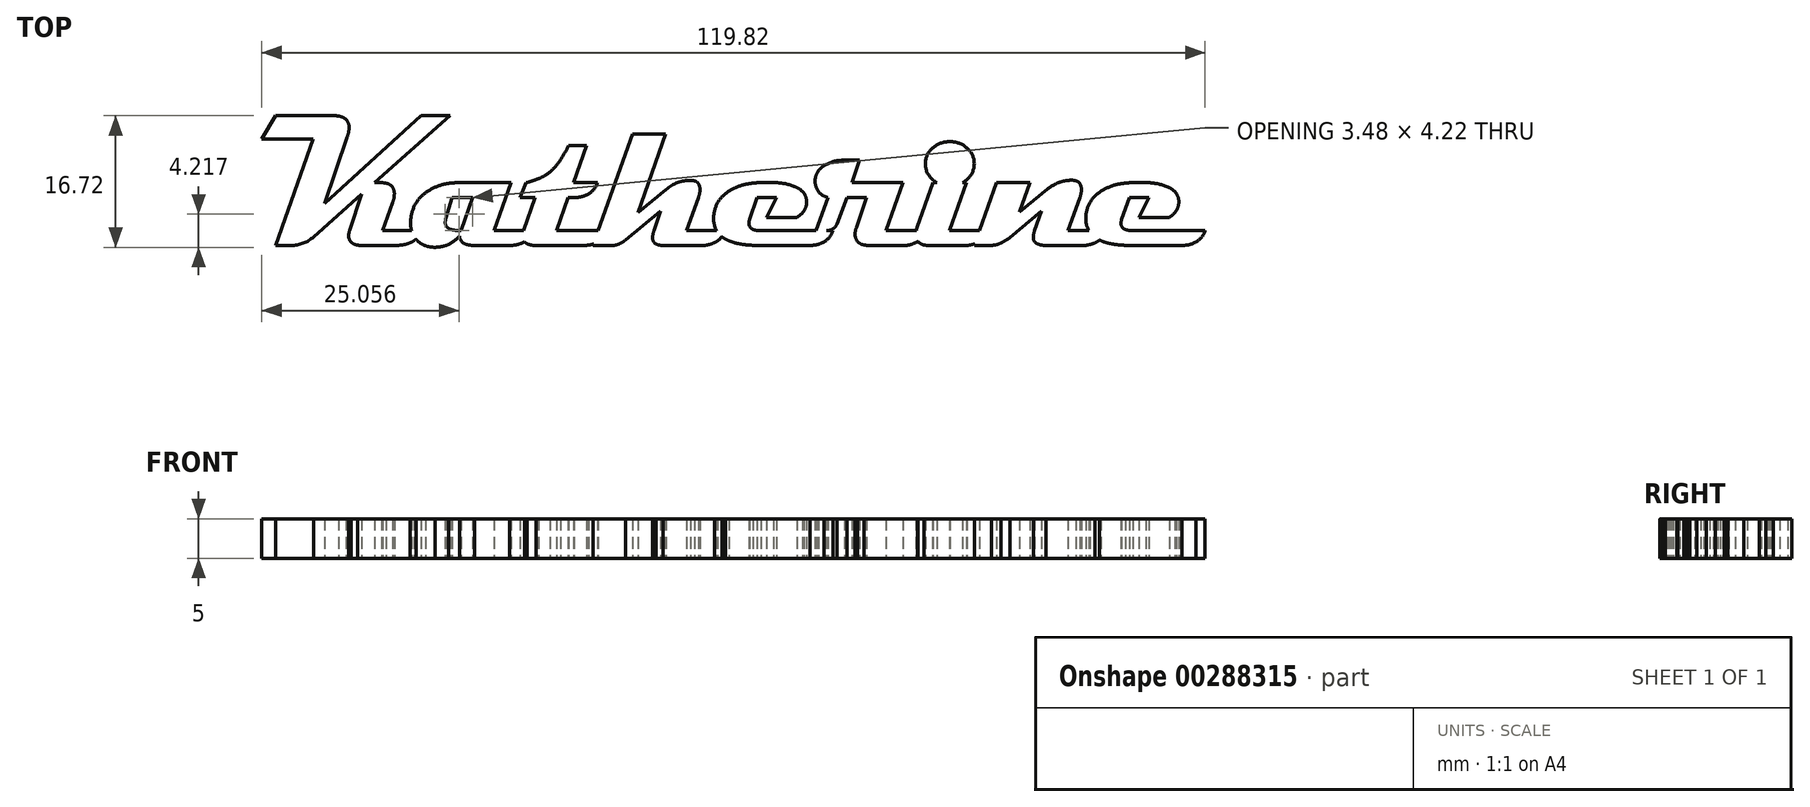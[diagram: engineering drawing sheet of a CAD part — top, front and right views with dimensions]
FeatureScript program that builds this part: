
annotation { "Feature Type Name" : "Feature", "Feature Type Description" : "" }
export const myFeature = defineFeature(function(context is Context, id is Id, definition is map)
    precondition{}
    {
        {
            var Q0;
            Q0=qCreatedBy(makeId("Top.planeOp"),FACE);
            var sketch = newSketch(context, id + "F0", { "sketchPlane" : qUnion([Q0])});
            skArc(sketch, "E0", {"start": v(-40.3, -7.32) * mm, "mid": v(-40.65, -7.59) * mm, "end": v(-41.04, -7.78) * mm});
            skArc(sketch, "E1", {"start": v(-41.04, -7.78) * mm, "mid": v(-41.53, -7.95) * mm, "end": v(-42.04, -8.06) * mm});
            skArc(sketch, "E2", {"start": v(-42.04, -8.06) * mm, "mid": v(-42.55, -8.11) * mm, "end": v(-43.07, -8.13) * mm});
            skLineSegment(sketch, "E3", {"start": v(-43.07, -8.13) * mm, "end": v(-47.17, -8.13) * mm});
            skArc(sketch, "E4", {"start": v(-47.17, -8.13) * mm, "mid": v(-47.46, -8.12) * mm, "end": v(-47.75, -8.08) * mm});
            skArc(sketch, "E5", {"start": v(-47.75, -8.08) * mm, "mid": v(-48.19, -7.96) * mm, "end": v(-48.56, -7.7) * mm});
            skArc(sketch, "E6", {"start": v(-48.56, -7.7) * mm, "mid": v(-48.8, -7.32) * mm, "end": v(-48.86, -6.87) * mm});
            skArc(sketch, "E7", {"start": v(-48.86, -6.87) * mm, "mid": v(-48.83, -6.56) * mm, "end": v(-48.75, -6.25) * mm});
            skLineSegment(sketch, "E8", {"start": v(-48.75, -6.25) * mm, "end": v(-47.2, -1.58) * mm});
            skLineSegment(sketch, "E9", {"start": v(-47.2, -1.58) * mm, "end": v(-53.31, -7.03) * mm});
            skArc(sketch, "E10", {"start": v(-53.31, -7.03) * mm, "mid": v(-54.64, -7.85) * mm, "end": v(-56.17, -8.13) * mm});
            skLineSegment(sketch, "E11", {"start": v(-56.17, -8.13) * mm, "end": v(-58.14, -8.13) * mm});
            skLineSegment(sketch, "E12", {"start": v(-58.14, -8.13) * mm, "end": v(-53.36, 5.4) * mm});
            skLineSegment(sketch, "E13", {"start": v(-53.36, 5.4) * mm, "end": v(-59.91, 5.4) * mm});
            skLineSegment(sketch, "E14", {"start": v(-59.91, 5.4) * mm, "end": v(-58.12, 8.36) * mm});
            skLineSegment(sketch, "E15", {"start": v(-58.12, 8.36) * mm, "end": v(-50.82, 8.36) * mm});
            skArc(sketch, "E16", {"start": v(-50.82, 8.36) * mm, "mid": v(-50.47, 8.35) * mm, "end": v(-50.12, 8.3) * mm});
            skArc(sketch, "E17", {"start": v(-50.12, 8.3) * mm, "mid": v(-49.6, 8.15) * mm, "end": v(-49.16, 7.85) * mm});
            skArc(sketch, "E18", {"start": v(-49.16, 7.85) * mm, "mid": v(-48.89, 7.38) * mm, "end": v(-48.81, 6.85) * mm});
            skArc(sketch, "E19", {"start": v(-48.81, 6.85) * mm, "mid": v(-48.88, 6.24) * mm, "end": v(-49.05, 5.65) * mm});
            skLineSegment(sketch, "E20", {"start": v(-49.05, 5.65) * mm, "end": v(-51.9, -2.8) * mm});
            skLineSegment(sketch, "E21", {"start": v(-51.9, -2.8) * mm, "end": v(-39.66, 8.36) * mm});
            skLineSegment(sketch, "E22", {"start": v(-39.66, 8.36) * mm, "end": v(-36, 8.36) * mm});
            skLineSegment(sketch, "E23", {"start": v(-36, 8.36) * mm, "end": v(-45.59, -0.16) * mm});
            skLineSegment(sketch, "E24", {"start": v(-45.59, -0.16) * mm, "end": v(-44.7, -0.16) * mm});
            skArc(sketch, "E25", {"start": v(-44.7, -0.16) * mm, "mid": v(-44.4, -0.17) * mm, "end": v(-44.09, -0.22) * mm});
            skArc(sketch, "E26", {"start": v(-44.09, -0.22) * mm, "mid": v(-43.65, -0.4) * mm, "end": v(-43.3, -0.7) * mm});
            skArc(sketch, "E27", {"start": v(-43.3, -0.7) * mm, "mid": v(-43.1, -1.13) * mm, "end": v(-43.06, -1.6) * mm});
            skArc(sketch, "E28", {"start": v(-43.06, -1.6) * mm, "mid": v(-43.12, -2.16) * mm, "end": v(-43.28, -2.7) * mm});
            skLineSegment(sketch, "E29", {"start": v(-43.28, -2.7) * mm, "end": v(-44.52, -6.25) * mm});
            skLineSegment(sketch, "E30", {"start": v(-44.52, -6.25) * mm, "end": v(-40.87, -6.25) * mm});
            skArc(sketch, "E31", {"start": v(-40.87, -6.25) * mm, "mid": v(-40.97, -5.79) * mm, "end": v(-40.99, -5.31) * mm});
            skArc(sketch, "E32", {"start": v(-40.99, -5.31) * mm, "mid": v(-40.88, -4.2) * mm, "end": v(-40.53, -3.15) * mm});
            skArc(sketch, "E33", {"start": v(-40.53, -3.15) * mm, "mid": v(-39.93, -2.21) * mm, "end": v(-39.11, -1.45) * mm});
            skArc(sketch, "E34", {"start": v(-39.11, -1.45) * mm, "mid": v(-38.16, -0.86) * mm, "end": v(-37.12, -0.45) * mm});
            skArc(sketch, "E35", {"start": v(-37.12, -0.45) * mm, "mid": v(-36.02, -0.23) * mm, "end": v(-34.9, -0.16) * mm});
            skLineSegment(sketch, "E36", {"start": v(-34.9, -0.16) * mm, "end": v(-28.21, -0.16) * mm});
            skLineSegment(sketch, "E37", {"start": v(-28.21, -0.16) * mm, "end": v(-30.42, -6.25) * mm});
            skLineSegment(sketch, "E38", {"start": v(-30.42, -6.25) * mm, "end": v(-26.66, -6.25) * mm});
            skLineSegment(sketch, "E39", {"start": v(-26.66, -6.25) * mm, "end": v(-25.17, -2.03) * mm});
            skLineSegment(sketch, "E40", {"start": v(-25.17, -2.03) * mm, "end": v(-27.1, -2.03) * mm});
            skLineSegment(sketch, "E41", {"start": v(-27.1, -2.03) * mm, "end": v(-26.36, -0.16) * mm});
            skArc(sketch, "E42", {"start": v(-26.36, -0.16) * mm, "mid": v(-25.55, 0.07) * mm, "end": v(-24.76, 0.36) * mm});
            skArc(sketch, "E43", {"start": v(-24.76, 0.36) * mm, "mid": v(-24, 0.72) * mm, "end": v(-23.3, 1.19) * mm});
            skArc(sketch, "E44", {"start": v(-23.3, 1.19) * mm, "mid": v(-22.58, 1.93) * mm, "end": v(-21.96, 2.76) * mm});
            skArc(sketch, "E45", {"start": v(-21.96, 2.76) * mm, "mid": v(-21.4, 3.64) * mm, "end": v(-20.9, 4.54) * mm});
            skLineSegment(sketch, "E46", {"start": v(-20.9, 4.54) * mm, "end": v(-18.62, 4.54) * mm});
            skLineSegment(sketch, "E47", {"start": v(-18.62, 4.54) * mm, "end": v(-20.27, -0.16) * mm});
            skLineSegment(sketch, "E48", {"start": v(-20.27, -0.16) * mm, "end": v(-17.25, -0.16) * mm});
            skArc(sketch, "E49", {"start": v(-17.25, -0.16) * mm, "mid": v(-17.7, -0.98) * mm, "end": v(-18.4, -1.6) * mm});
            skArc(sketch, "E50", {"start": v(-18.4, -1.6) * mm, "mid": v(-19.28, -1.94) * mm, "end": v(-20.2, -2.03) * mm});
            skLineSegment(sketch, "E51", {"start": v(-20.2, -2.03) * mm, "end": v(-20.98, -2.03) * mm});
            skLineSegment(sketch, "E52", {"start": v(-20.98, -2.03) * mm, "end": v(-22.44, -6.25) * mm});
            skLineSegment(sketch, "E53", {"start": v(-22.44, -6.25) * mm, "end": v(-17.16, -6.25) * mm});
            skLineSegment(sketch, "E54", {"start": v(-17.16, -6.25) * mm, "end": v(-12.81, 6.03) * mm});
            skLineSegment(sketch, "E55", {"start": v(-12.81, 6.03) * mm, "end": v(-8.6, 6.03) * mm});
            skLineSegment(sketch, "E56", {"start": v(-8.6, 6.03) * mm, "end": v(-12.12, -3.93) * mm});
            skLineSegment(sketch, "E57", {"start": v(-12.12, -3.93) * mm, "end": v(-8.55, -1) * mm});
            skArc(sketch, "E58", {"start": v(-8.55, -1) * mm, "mid": v(-7.08, -0.15) * mm, "end": v(-5.4, 0.13) * mm});
            skArc(sketch, "E59", {"start": v(-5.4, 0.13) * mm, "mid": v(-5.17, 0.12) * mm, "end": v(-4.93, 0.07) * mm});
            skArc(sketch, "E60", {"start": v(-4.93, 0.07) * mm, "mid": v(-4.61, -0.1) * mm, "end": v(-4.38, -0.37) * mm});
            skArc(sketch, "E61", {"start": v(-4.38, -0.37) * mm, "mid": v(-4.26, -0.7) * mm, "end": v(-4.23, -1.06) * mm});
            skArc(sketch, "E62", {"start": v(-4.23, -1.06) * mm, "mid": v(-4.3, -1.57) * mm, "end": v(-4.45, -2.06) * mm});
            skLineSegment(sketch, "E63", {"start": v(-4.45, -2.06) * mm, "end": v(-5.93, -6.25) * mm});
            skLineSegment(sketch, "E64", {"start": v(-5.93, -6.25) * mm, "end": v(-2.12, -6.25) * mm});
            skArc(sketch, "E65", {"start": v(-2.12, -6.25) * mm, "mid": v(-2.12, -6.25) * mm, "end": v(-2.12, -6.24) * mm});
            skArc(sketch, "E66", {"start": v(-2.12, -6.24) * mm, "mid": v(-2.42, -5.5) * mm, "end": v(-2.5, -4.7) * mm});
            skArc(sketch, "E67", {"start": v(-2.5, -4.7) * mm, "mid": v(-2.39, -3.66) * mm, "end": v(-2, -2.7) * mm});
            skArc(sketch, "E68", {"start": v(-2, -2.7) * mm, "mid": v(-1.37, -1.88) * mm, "end": v(-0.56, -1.24) * mm});
            skArc(sketch, "E69", {"start": v(-0.56, -1.24) * mm, "mid": v(0.36, -0.74) * mm, "end": v(1.35, -0.4) * mm});
            skArc(sketch, "E70", {"start": v(1.35, -0.4) * mm, "mid": v(2.38, -0.22) * mm, "end": v(3.43, -0.16) * mm});
            skLineSegment(sketch, "E71", {"start": v(3.43, -0.16) * mm, "end": v(5.12, -0.16) * mm});
            skArc(sketch, "E72", {"start": v(5.13, -0.16) * mm, "mid": v(6.45, -0.26) * mm, "end": v(7.74, -0.62) * mm});
            skArc(sketch, "E73", {"start": v(7.74, -0.62) * mm, "mid": v(8.3, -0.9) * mm, "end": v(8.8, -1.3) * mm});
            skArc(sketch, "E74", {"start": v(8.8, -1.3) * mm, "mid": v(9.16, -1.84) * mm, "end": v(9.3, -2.47) * mm});
            skArc(sketch, "E75", {"start": v(9.3, -2.47) * mm, "mid": v(9.25, -3.1) * mm, "end": v(9, -3.68) * mm});
            skArc(sketch, "E76", {"start": v(9, -3.68) * mm, "mid": v(8.6, -4.16) * mm, "end": v(8.1, -4.55) * mm});
            skLineSegment(sketch, "E77", {"start": v(8.1, -4.55) * mm, "end": v(4.22, -4.55) * mm});
            skLineSegment(sketch, "E78", {"start": v(4.22, -4.55) * mm, "end": v(5.49, -2.03) * mm});
            skLineSegment(sketch, "E79", {"start": v(5.49, -2.03) * mm, "end": v(3.02, -2.03) * mm});
            skLineSegment(sketch, "E80", {"start": v(3.02, -2.03) * mm, "end": v(2.05, -4.86) * mm});
            skArc(sketch, "E81", {"start": v(2.05, -4.86) * mm, "mid": v(2, -5.08) * mm, "end": v(1.97, -5.3) * mm});
            skArc(sketch, "E82", {"start": v(1.97, -5.3) * mm, "mid": v(2.12, -5.8) * mm, "end": v(2.53, -6.1) * mm});
            skArc(sketch, "E83", {"start": v(2.53, -6.1) * mm, "mid": v(3, -6.22) * mm, "end": v(3.5, -6.25) * mm});
            skLineSegment(sketch, "E84", {"start": v(3.5, -6.25) * mm, "end": v(10.48, -6.25) * mm});
            skLineSegment(sketch, "E85", {"start": v(10.48, -6.25) * mm, "end": v(12.02, -2.03) * mm});
            skArc(sketch, "E86", {"start": v(12.02, -2.03) * mm, "mid": v(11.36, -1.77) * mm, "end": v(10.84, -1.3) * mm});
            skArc(sketch, "E87", {"start": v(10.84, -1.3) * mm, "mid": v(10.5, -0.69) * mm, "end": v(10.4, 0) * mm});
            skArc(sketch, "E88", {"start": v(10.4, 0) * mm, "mid": v(10.47, 0.64) * mm, "end": v(10.72, 1.23) * mm});
            skArc(sketch, "E89", {"start": v(10.72, 1.23) * mm, "mid": v(11.13, 1.72) * mm, "end": v(11.64, 2.1) * mm});
            skArc(sketch, "E90", {"start": v(11.64, 2.1) * mm, "mid": v(12.85, 2.56) * mm, "end": v(14.13, 2.7) * mm});
            skLineSegment(sketch, "E91", {"start": v(14.13, 2.7) * mm, "end": v(16.03, 2.7) * mm});
            skLineSegment(sketch, "E92", {"start": v(16.03, 2.7) * mm, "end": v(15.04, -0.16) * mm});
            skLineSegment(sketch, "E93", {"start": v(15.04, -0.16) * mm, "end": v(21.52, -0.16) * mm});
            skLineSegment(sketch, "E94", {"start": v(21.52, -0.16) * mm, "end": v(19.4, -6.25) * mm});
            skLineSegment(sketch, "E95", {"start": v(19.4, -6.25) * mm, "end": v(23.22, -6.25) * mm});
            skArc(sketch, "E96", {"start": v(23.22, -6.25) * mm, "mid": v(23.27, -6.06) * mm, "end": v(23.34, -5.87) * mm});
            skLineSegment(sketch, "E97", {"start": v(23.34, -5.87) * mm, "end": v(25.38, -0.16) * mm});
            skLineSegment(sketch, "E98", {"start": v(25.38, -0.16) * mm, "end": v(25.89, -0.16) * mm});
            skArc(sketch, "E99", {"start": v(25.89, -0.16) * mm, "mid": v(25.58, 0.04) * mm, "end": v(25.3, 0.27) * mm});
            skArc(sketch, "E100", {"start": v(25.3, 0.27) * mm, "mid": v(24.62, 1.16) * mm, "end": v(24.4, 2.26) * mm});
            skArc(sketch, "E101", {"start": v(24.4, 2.26) * mm, "mid": v(24.62, 3.35) * mm, "end": v(25.3, 4.24) * mm});
            skArc(sketch, "E102", {"start": v(25.3, 4.24) * mm, "mid": v(26.32, 4.86) * mm, "end": v(27.5, 5.06) * mm});
            skArc(sketch, "E103", {"start": v(27.5, 5.06) * mm, "mid": v(28.68, 4.86) * mm, "end": v(29.69, 4.24) * mm});
            skArc(sketch, "E104", {"start": v(29.69, 4.24) * mm, "mid": v(30.37, 3.35) * mm, "end": v(30.6, 2.26) * mm});
            skArc(sketch, "E105", {"start": v(30.6, 2.26) * mm, "mid": v(30.37, 1.16) * mm, "end": v(29.69, 0.27) * mm});
            skArc(sketch, "E106", {"start": v(29.69, 0.27) * mm, "mid": v(29.4, 0.04) * mm, "end": v(29.1, -0.16) * mm});
            skLineSegment(sketch, "E107", {"start": v(29.1, -0.16) * mm, "end": v(29.63, -0.16) * mm});
            skLineSegment(sketch, "E108", {"start": v(29.63, -0.16) * mm, "end": v(27.46, -6.25) * mm});
            skLineSegment(sketch, "E109", {"start": v(27.46, -6.25) * mm, "end": v(31.3, -6.25) * mm});
            skLineSegment(sketch, "E110", {"start": v(31.3, -6.25) * mm, "end": v(33.43, -0.16) * mm});
            skLineSegment(sketch, "E111", {"start": v(33.43, -0.16) * mm, "end": v(37.66, -0.16) * mm});
            skLineSegment(sketch, "E112", {"start": v(37.66, -0.16) * mm, "end": v(36.34, -3.9) * mm});
            skLineSegment(sketch, "E113", {"start": v(36.34, -3.9) * mm, "end": v(39.91, -0.98) * mm});
            skArc(sketch, "E114", {"start": v(39.91, -0.98) * mm, "mid": v(40.61, -0.49) * mm, "end": v(41.39, -0.12) * mm});
            skArc(sketch, "E115", {"start": v(41.39, -0.12) * mm, "mid": v(42.21, 0.1) * mm, "end": v(43.07, 0.16) * mm});
            skArc(sketch, "E116", {"start": v(43.07, 0.16) * mm, "mid": v(43.3, 0.13) * mm, "end": v(43.53, 0.08) * mm});
            skArc(sketch, "E117", {"start": v(43.53, 0.08) * mm, "mid": v(43.85, -0.1) * mm, "end": v(44.07, -0.37) * mm});
            skArc(sketch, "E118", {"start": v(44.07, -0.37) * mm, "mid": v(44.18, -0.7) * mm, "end": v(44.21, -1.06) * mm});
            skArc(sketch, "E119", {"start": v(44.21, -1.06) * mm, "mid": v(44.16, -1.55) * mm, "end": v(44.03, -2.03) * mm});
            skLineSegment(sketch, "E120", {"start": v(44.03, -2.03) * mm, "end": v(42.52, -6.25) * mm});
            skLineSegment(sketch, "E121", {"start": v(42.52, -6.25) * mm, "end": v(45.16, -6.25) * mm});
            skArc(sketch, "E122", {"start": v(45.16, -6.25) * mm, "mid": v(45.15, -6.25) * mm, "end": v(45.15, -6.24) * mm});
            skArc(sketch, "E123", {"start": v(45.15, -6.24) * mm, "mid": v(44.86, -5.5) * mm, "end": v(44.77, -4.7) * mm});
            skArc(sketch, "E124", {"start": v(44.77, -4.7) * mm, "mid": v(44.89, -3.66) * mm, "end": v(45.27, -2.7) * mm});
            skArc(sketch, "E125", {"start": v(45.27, -2.7) * mm, "mid": v(45.9, -1.88) * mm, "end": v(46.71, -1.24) * mm});
            skArc(sketch, "E126", {"start": v(46.71, -1.24) * mm, "mid": v(47.64, -0.74) * mm, "end": v(48.63, -0.4) * mm});
            skArc(sketch, "E127", {"start": v(48.63, -0.4) * mm, "mid": v(49.66, -0.22) * mm, "end": v(50.7, -0.16) * mm});
            skLineSegment(sketch, "E128", {"start": v(50.7, -0.16) * mm, "end": v(52.4, -0.16) * mm});
            skArc(sketch, "E129", {"start": v(52.4, -0.16) * mm, "mid": v(53.73, -0.26) * mm, "end": v(55.01, -0.62) * mm});
            skArc(sketch, "E130", {"start": v(55.01, -0.62) * mm, "mid": v(55.58, -0.9) * mm, "end": v(56.08, -1.3) * mm});
            skArc(sketch, "E131", {"start": v(56.08, -1.3) * mm, "mid": v(56.44, -1.84) * mm, "end": v(56.58, -2.47) * mm});
            skArc(sketch, "E132", {"start": v(56.58, -2.47) * mm, "mid": v(56.52, -3.1) * mm, "end": v(56.27, -3.68) * mm});
            skArc(sketch, "E133", {"start": v(56.27, -3.68) * mm, "mid": v(55.87, -4.16) * mm, "end": v(55.38, -4.55) * mm});
            skLineSegment(sketch, "E134", {"start": v(55.38, -4.55) * mm, "end": v(51.5, -4.55) * mm});
            skLineSegment(sketch, "E135", {"start": v(51.5, -4.55) * mm, "end": v(52.76, -2.03) * mm});
            skLineSegment(sketch, "E136", {"start": v(52.76, -2.03) * mm, "end": v(50.29, -2.03) * mm});
            skLineSegment(sketch, "E137", {"start": v(50.29, -2.03) * mm, "end": v(49.33, -4.86) * mm});
            skArc(sketch, "E138", {"start": v(49.33, -4.86) * mm, "mid": v(49.27, -5.08) * mm, "end": v(49.25, -5.3) * mm});
            skArc(sketch, "E139", {"start": v(49.25, -5.3) * mm, "mid": v(49.4, -5.8) * mm, "end": v(49.8, -6.1) * mm});
            skArc(sketch, "E140", {"start": v(49.8, -6.1) * mm, "mid": v(50.28, -6.22) * mm, "end": v(50.77, -6.25) * mm});
            skLineSegment(sketch, "E141", {"start": v(50.77, -6.25) * mm, "end": v(59.91, -6.25) * mm});
            skArc(sketch, "E142", {"start": v(59.91, -6.25) * mm, "mid": v(59.5, -7.08) * mm, "end": v(58.79, -7.67) * mm});
            skArc(sketch, "E143", {"start": v(58.79, -7.67) * mm, "mid": v(57.92, -8.02) * mm, "end": v(57, -8.13) * mm});
            skLineSegment(sketch, "E144", {"start": v(57, -8.13) * mm, "end": v(50.46, -8.13) * mm});
            skArc(sketch, "E145", {"start": v(50.46, -8.13) * mm, "mid": v(49.56, -8.1) * mm, "end": v(48.66, -8.02) * mm});
            skArc(sketch, "E146", {"start": v(48.66, -8.02) * mm, "mid": v(47.97, -7.91) * mm, "end": v(47.3, -7.74) * mm});
            skArc(sketch, "E147", {"start": v(47.3, -7.74) * mm, "mid": v(46.9, -7.6) * mm, "end": v(46.51, -7.44) * mm});
            skArc(sketch, "E148", {"start": v(46.51, -7.44) * mm, "mid": v(46.25, -7.63) * mm, "end": v(45.96, -7.78) * mm});
            skArc(sketch, "E149", {"start": v(45.96, -7.78) * mm, "mid": v(45.19, -8.04) * mm, "end": v(44.38, -8.13) * mm});
            skLineSegment(sketch, "E150", {"start": v(44.38, -8.13) * mm, "end": v(39.7, -8.13) * mm});
            skArc(sketch, "E151", {"start": v(39.7, -8.13) * mm, "mid": v(39.18, -8.1) * mm, "end": v(38.67, -7.95) * mm});
            skArc(sketch, "E152", {"start": v(38.67, -7.95) * mm, "mid": v(38.24, -7.6) * mm, "end": v(38.1, -7.07) * mm});
            skArc(sketch, "E153", {"start": v(38.1, -7.07) * mm, "mid": v(38.15, -6.66) * mm, "end": v(38.26, -6.25) * mm});
            skLineSegment(sketch, "E154", {"start": v(38.26, -6.25) * mm, "end": v(39.15, -3.73) * mm});
            skLineSegment(sketch, "E155", {"start": v(39.15, -3.73) * mm, "end": v(35.12, -7.14) * mm});
            skArc(sketch, "E156", {"start": v(35.12, -7.14) * mm, "mid": v(34.58, -7.5) * mm, "end": v(34.02, -7.8) * mm});
            skArc(sketch, "E157", {"start": v(34.02, -7.8) * mm, "mid": v(33.42, -8.03) * mm, "end": v(32.79, -8.13) * mm});
            skLineSegment(sketch, "E158", {"start": v(32.79, -8.13) * mm, "end": v(30.63, -8.13) * mm});
            skLineSegment(sketch, "E159", {"start": v(30.63, -8.13) * mm, "end": v(30.71, -7.9) * mm});
            skArc(sketch, "E160", {"start": v(30.71, -7.9) * mm, "mid": v(30.1, -8.07) * mm, "end": v(29.48, -8.13) * mm});
            skLineSegment(sketch, "E161", {"start": v(29.48, -8.13) * mm, "end": v(24.85, -8.13) * mm});
            skArc(sketch, "E162", {"start": v(24.85, -8.13) * mm, "mid": v(24.54, -8.11) * mm, "end": v(24.23, -8.07) * mm});
            skArc(sketch, "E163", {"start": v(24.23, -8.07) * mm, "mid": v(23.8, -7.91) * mm, "end": v(23.43, -7.61) * mm});
            skArc(sketch, "E164", {"start": v(23.43, -7.61) * mm, "mid": v(23.42, -7.62) * mm, "end": v(23.4, -7.63) * mm});
            skArc(sketch, "E165", {"start": v(23.4, -7.63) * mm, "mid": v(22.6, -8) * mm, "end": v(21.73, -8.13) * mm});
            skLineSegment(sketch, "E166", {"start": v(21.73, -8.13) * mm, "end": v(17.25, -8.13) * mm});
            skArc(sketch, "E167", {"start": v(17.25, -8.13) * mm, "mid": v(16.92, -8.11) * mm, "end": v(16.6, -8.07) * mm});
            skArc(sketch, "E168", {"start": v(16.6, -8.07) * mm, "mid": v(16.13, -7.9) * mm, "end": v(15.74, -7.59) * mm});
            skArc(sketch, "E169", {"start": v(15.74, -7.59) * mm, "mid": v(15.52, -7.14) * mm, "end": v(15.46, -6.65) * mm});
            skArc(sketch, "E170", {"start": v(15.46, -6.65) * mm, "mid": v(15.5, -6.24) * mm, "end": v(15.62, -5.84) * mm});
            skLineSegment(sketch, "E171", {"start": v(15.62, -5.84) * mm, "end": v(16.94, -2.03) * mm});
            skLineSegment(sketch, "E172", {"start": v(16.94, -2.03) * mm, "end": v(14.45, -2.03) * mm});
            skLineSegment(sketch, "E173", {"start": v(14.45, -2.03) * mm, "end": v(13.14, -5.4) * mm});
            skArc(sketch, "E174", {"start": v(13.14, -5.4) * mm, "mid": v(12.92, -5.78) * mm, "end": v(12.58, -6.06) * mm});
            skArc(sketch, "E175", {"start": v(12.58, -6.06) * mm, "mid": v(12.22, -6.2) * mm, "end": v(11.84, -6.25) * mm});
            skLineSegment(sketch, "E176", {"start": v(11.84, -6.25) * mm, "end": v(12.64, -6.25) * mm});
            skArc(sketch, "E177", {"start": v(12.64, -6.25) * mm, "mid": v(12.22, -7.08) * mm, "end": v(11.51, -7.67) * mm});
            skArc(sketch, "E178", {"start": v(11.51, -7.67) * mm, "mid": v(10.65, -8.02) * mm, "end": v(9.72, -8.13) * mm});
            skLineSegment(sketch, "E179", {"start": v(9.72, -8.13) * mm, "end": v(3.2, -8.13) * mm});
            skArc(sketch, "E180", {"start": v(3.2, -8.13) * mm, "mid": v(2.29, -8.1) * mm, "end": v(1.38, -8.02) * mm});
            skArc(sketch, "E181", {"start": v(1.38, -8.02) * mm, "mid": v(0.7, -7.91) * mm, "end": v(0.02, -7.74) * mm});
            skArc(sketch, "E182", {"start": v(0.02, -7.74) * mm, "mid": v(-0.48, -7.57) * mm, "end": v(-0.96, -7.34) * mm});
            skArc(sketch, "E183", {"start": v(-0.96, -7.34) * mm, "mid": v(-1.22, -7.18) * mm, "end": v(-1.47, -7) * mm});
            skArc(sketch, "E184", {"start": v(-1.47, -7) * mm, "mid": v(-1.89, -7.45) * mm, "end": v(-2.4, -7.78) * mm});
            skArc(sketch, "E185", {"start": v(-2.4, -7.78) * mm, "mid": v(-3.15, -8.04) * mm, "end": v(-3.94, -8.13) * mm});
            skLineSegment(sketch, "E186", {"start": v(-3.94, -8.13) * mm, "end": v(-8.93, -8.13) * mm});
            skArc(sketch, "E187", {"start": v(-8.93, -8.13) * mm, "mid": v(-9.39, -8.1) * mm, "end": v(-9.82, -7.95) * mm});
            skArc(sketch, "E188", {"start": v(-9.82, -7.95) * mm, "mid": v(-10.16, -7.63) * mm, "end": v(-10.26, -7.17) * mm});
            skArc(sketch, "E189", {"start": v(-10.26, -7.17) * mm, "mid": v(-10.2, -6.7) * mm, "end": v(-10.08, -6.25) * mm});
            skLineSegment(sketch, "E190", {"start": v(-10.08, -6.25) * mm, "end": v(-9.24, -3.76) * mm});
            skLineSegment(sketch, "E191", {"start": v(-9.24, -3.76) * mm, "end": v(-13.68, -7.41) * mm});
            skArc(sketch, "E192", {"start": v(-13.68, -7.41) * mm, "mid": v(-14.06, -7.7) * mm, "end": v(-14.48, -7.93) * mm});
            skArc(sketch, "E193", {"start": v(-14.48, -7.93) * mm, "mid": v(-14.94, -8.08) * mm, "end": v(-15.41, -8.13) * mm});
            skLineSegment(sketch, "E194", {"start": v(-15.41, -8.13) * mm, "end": v(-17.83, -8.13) * mm});
            skLineSegment(sketch, "E195", {"start": v(-17.83, -8.13) * mm, "end": v(-17.76, -7.94) * mm});
            skArc(sketch, "E196", {"start": v(-17.76, -7.94) * mm, "mid": v(-17.95, -8) * mm, "end": v(-18.15, -8.04) * mm});
            skArc(sketch, "E197", {"start": v(-18.15, -8.04) * mm, "mid": v(-18.61, -8.1) * mm, "end": v(-19.08, -8.13) * mm});
            skLineSegment(sketch, "E198", {"start": v(-19.08, -8.13) * mm, "end": v(-25.05, -8.13) * mm});
            skArc(sketch, "E199", {"start": v(-25.05, -8.13) * mm, "mid": v(-25.64, -8.08) * mm, "end": v(-26.2, -7.91) * mm});
            skArc(sketch, "E200", {"start": v(-26.2, -7.91) * mm, "mid": v(-26.39, -7.8) * mm, "end": v(-26.54, -7.65) * mm});
            skArc(sketch, "E201", {"start": v(-26.54, -7.65) * mm, "mid": v(-26.8, -7.8) * mm, "end": v(-27.06, -7.91) * mm});
            skArc(sketch, "E202", {"start": v(-27.06, -7.91) * mm, "mid": v(-27.74, -8.08) * mm, "end": v(-28.43, -8.13) * mm});
            skLineSegment(sketch, "E203", {"start": v(-28.43, -8.13) * mm, "end": v(-32.87, -8.13) * mm});
            skArc(sketch, "E204", {"start": v(-32.87, -8.13) * mm, "mid": v(-33.48, -8.09) * mm, "end": v(-34.08, -7.93) * mm});
            skArc(sketch, "E205", {"start": v(-34.08, -7.93) * mm, "mid": v(-34.6, -7.53) * mm, "end": v(-34.77, -6.9) * mm});
            skArc(sketch, "E206", {"start": v(-34.77, -6.9) * mm, "mid": v(-35.41, -7.52) * mm, "end": v(-36.17, -7.99) * mm});
            skArc(sketch, "E207", {"start": v(-36.17, -7.99) * mm, "mid": v(-37.02, -8.27) * mm, "end": v(-37.9, -8.36) * mm});
            skArc(sketch, "E208", {"start": v(-37.9, -8.36) * mm, "mid": v(-38.51, -8.32) * mm, "end": v(-39.1, -8.17) * mm});
            skArc(sketch, "E209", {"start": v(-39.1, -8.17) * mm, "mid": v(-39.65, -7.9) * mm, "end": v(-40.13, -7.52) * mm});
            skArc(sketch, "E210", {"start": v(-40.13, -7.52) * mm, "mid": v(-40.22, -7.42) * mm, "end": v(-40.3, -7.32) * mm});
            skLineSegment(sketch, "E211", {"start": v(-33.11, -2.03) * mm, "end": v(-35.7, -2.03) * mm});
            skLineSegment(sketch, "E212", {"start": v(-35.7, -2.03) * mm, "end": v(-36.52, -4.76) * mm});
            skArc(sketch, "E213", {"start": v(-36.52, -4.76) * mm, "mid": v(-36.57, -5) * mm, "end": v(-36.6, -5.23) * mm});
            skArc(sketch, "E214", {"start": v(-36.6, -5.23) * mm, "mid": v(-36.54, -5.55) * mm, "end": v(-36.35, -5.82) * mm});
            skArc(sketch, "E215", {"start": v(-36.35, -5.82) * mm, "mid": v(-36.17, -5.96) * mm, "end": v(-35.96, -6.06) * mm});
            skArc(sketch, "E216", {"start": v(-35.96, -6.06) * mm, "mid": v(-35.63, -6.16) * mm, "end": v(-35.29, -6.21) * mm});
            skArc(sketch, "E217", {"start": v(-35.29, -6.21) * mm, "mid": v(-34.95, -6.24) * mm, "end": v(-34.6, -6.25) * mm});
            skLineSegment(sketch, "E218", {"start": v(-34.6, -6.25) * mm, "end": v(-33.11, -2.03) * mm});
            skSolve(sketch);
        }
        {
            var Q0;
            Q0 = qSketchRegion(id + "F0", true);
            extrude(context, id + "F1", {"entities" : qUnion([Q0]), "depth" : 5 * mm});
        }
    });
